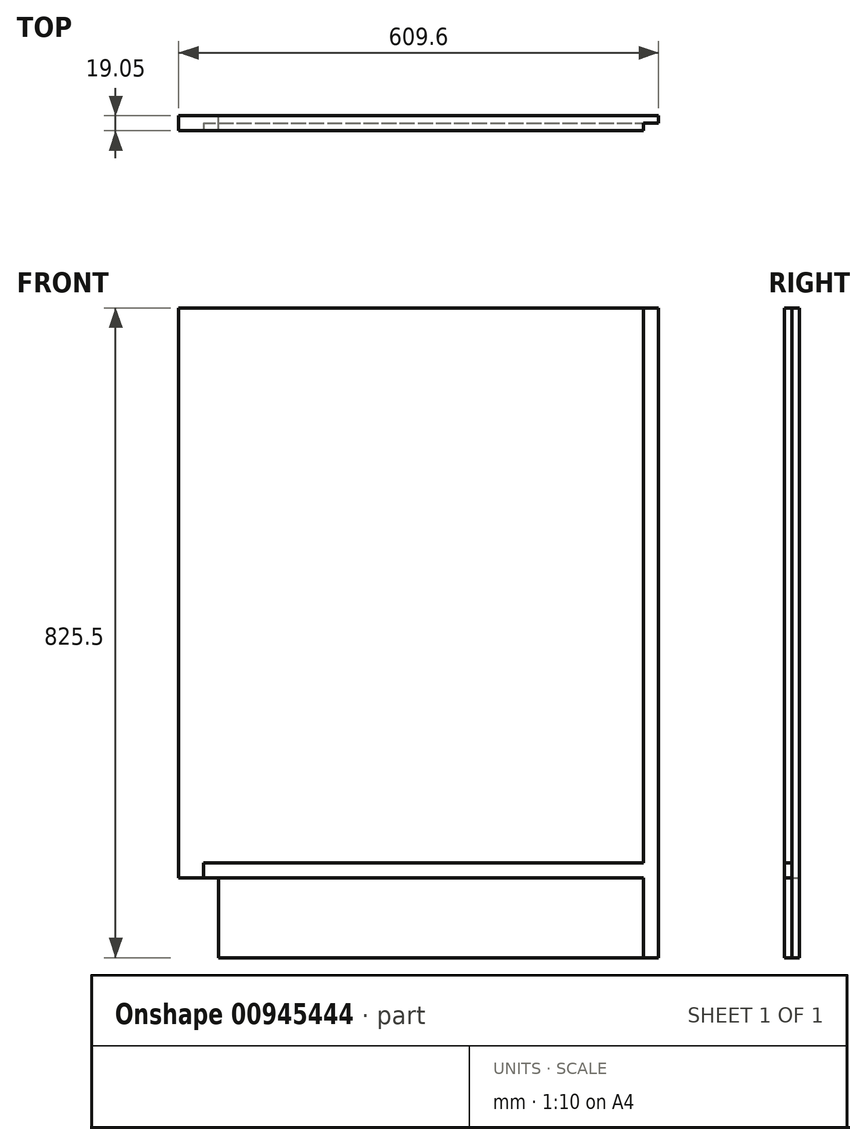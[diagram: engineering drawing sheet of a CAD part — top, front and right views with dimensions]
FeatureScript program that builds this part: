
annotation { "Feature Type Name" : "Feature", "Feature Type Description" : "" }
export const myFeature = defineFeature(function(context is Context, id is Id, definition is map)
    precondition{}
    {
        {
            var Q0;
            Q0=qCreatedBy(makeId("Front.planeOp"),FACE);
            var sketch = newSketch(context, id + "F0", { "sketchPlane" : qUnion([Q0])});
            skLineSegment(sketch, "E0.bottom", {"start": v(0, 0) * mm, "end": v(-558.8, 0) * mm});
            skLineSegment(sketch, "E0.top", {"start": v(0, 825.5) * mm, "end": v(-609.6, 825.5) * mm});
            skLineSegment(sketch, "E0.left", {"start": v(0, 0) * mm, "end": v(0, 825.5) * mm});
            skLineSegment(sketch, "E0.right", {"start": v(-609.6, 101.6) * mm, "end": v(-609.6, 825.5) * mm});
            skLineSegment(sketch, "E1", {"start": v(-609.6, 101.6) * mm, "end": v(-558.8, 101.6) * mm});
            skLineSegment(sketch, "E2", {"start": v(-558.8, 101.6) * mm, "end": v(-558.8, 0) * mm});
            skSolve(sketch);
        }
        {
            var Q0;
            Q0=makeQuery(id+"F0.imprint","IMPRINT",FACE,{"disambiguationData":[TD([[makeQuery(id+"F0.imprint","IMPRINT",EDGE,{"derivedFrom":sQuery(id+"F0.wireOp",EDGE,"E0.bottom")}),-1.0]])]});
            extrude(context, id + "F1", {"entities" : qUnion([Q0]), "depth" : 19.05 * mm, "offsetDistance" : 25.4 * mm});
        }
        {
            var Q0;
            Q0=makeQuery(id+"F1.opExtrude","CAP_FACE",FACE,{"disambiguationData":[OSD([sQuery(id+"F0.wireOp",EDGE,"E0.bottom"),sQuery(id+"F0.wireOp",EDGE,"E0.top"),sQuery(id+"F0.wireOp",EDGE,"E0.left"),sQuery(id+"F0.wireOp",EDGE,"E0.right"),sQuery(id+"F0.wireOp",EDGE,"E1"),sQuery(id+"F0.wireOp",EDGE,"E2")])],"isStart":false});
            var sketch = newSketch(context, id + "F2", { "sketchPlane" : qUnion([Q0])});
            skLineSegment(sketch, "E3", {"start": v(-19.05, 825.5) * mm, "end": v(0, 825.5) * mm});
            skLineSegment(sketch, "E4", {"start": v(0, 0) * mm, "end": v(-19.05, 0) * mm});
            skLineSegment(sketch, "E5", {"start": v(-19.05, 0) * mm, "end": v(-19.05, 101.6) * mm});
            skLineSegment(sketch, "E6", {"start": v(-19.05, 101.6) * mm, "end": v(-577.85, 101.6) * mm});
            skLineSegment(sketch, "E7", {"start": v(-577.85, 101.6) * mm, "end": v(-577.85, 120.65) * mm});
            skLineSegment(sketch, "E8", {"start": v(-577.85, 120.65) * mm, "end": v(-19.05, 120.65) * mm});
            skLineSegment(sketch, "E9", {"start": v(-19.05, 120.65) * mm, "end": v(-19.05, 825.5) * mm});
            skSolve(sketch);
        }
        {
            var Q0;
            Q0=qSketchRegion(id+"F2",true);
            var Q1;
            Q1=makeQuery(id+"F2.imprint","IMPRINT",FACE,{"disambiguationData":[TD([[makeQuery(id+"F2.imprint","IMPRINT",EDGE,{"derivedFrom":sQuery(id+"F2.wireOp",EDGE,"E3")}),1.0]])]});
            extrude(context, id + "F3", {"entities" : qUnion([Q0, Q1]), "operationType" : NewBodyOperationType.REMOVE, "oppositeDirection" : true, "depth" : 9.52 * mm, "offsetDistance" : 25.4 * mm});
        }
    });
